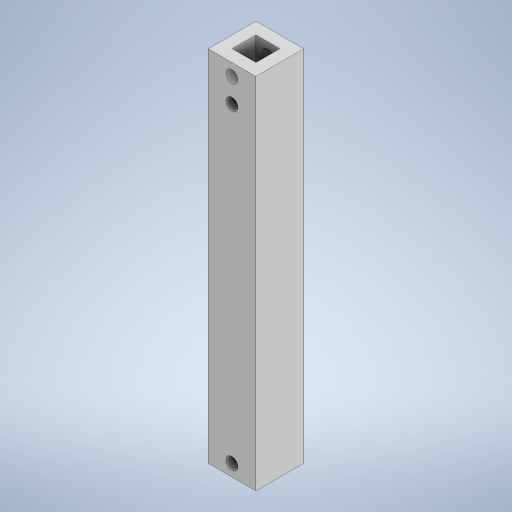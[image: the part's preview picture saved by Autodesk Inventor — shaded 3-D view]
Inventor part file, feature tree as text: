
AUTODESK INVENTOR PART (.ipt)
format: ipt  version: 2023 (Build 270158000, 158)  size: 249,856 bytes
history: native  units: mm
features: extrude x2, sketch x2
ambient origin geometry x8: Origin, YZ Plane, XZ Plane, XY Plane, X Axis, Y Axis, Z Axis, Center Point
bodies: Solido1 (feature_tree)
feature tree (4):
  extrude  "Estrusione1"  Depth=20.0mm
  extrude  "Estrusione2"  Depth=5.0mm
  sketch  "Schizzo2"
  sketch  "Schizzo3"
